# Revit family: MCBII
name_source: partatom
category: 機械設備
units: mm (PartAtom-declared; Revit-internal decimal feet)

## family parameters
OmniClass タイトル = Climate Control (HVAC)
OmniClass 番号 = 23.75.00.00
パーツ タイプ = 標準
ロード時にボイドで切り取り = いいえ
丸型コネクタ寸法 = 直径を使用
作業面ベース = いいえ
共有 = いいえ
常に垂直 = はい
部屋計算ポイント = いいえ

## types (11) — shared parameters
閉（開） = はい
zero-valued in all types: 既定の高さ

## per-type parameters (varying)
| type | H | W | l | t |
| C40x20x10x1.6 | 20  [stored 0.0656168 ft] | 40  [stored 0.131234 ft] | 10  [stored 0.0328084 ft] | 2  [stored 0.00656168 ft] |
| C45x30x10x1.4 | 30  [stored 0.0984252 ft] | 45  [stored 0.147638 ft] | 10  [stored 0.0328084 ft] | 1  [stored 0.00328084 ft] |
| C50x30x10x1.4 | 30  [stored 0.0984252 ft] | 50  [stored 0.164042 ft] | 10  [stored 0.0328084 ft] | 1  [stored 0.00328084 ft] |
| C60x30x10x1.4 | 30  [stored 0.0984252 ft] | 60  [stored 0.19685 ft] | 10  [stored 0.0328084 ft] | 1  [stored 0.00328084 ft] |
| C60x30x10x2.3 | 30  [stored 0.0984252 ft] | 60  [stored 0.19685 ft] | 10  [stored 0.0328084 ft] | 2  [stored 0.00656168 ft] |
| C65x30x10x1.4 | 30  [stored 0.0984252 ft] | 65  [stored 0.213255 ft] | 10  [stored 0.0328084 ft] | 1  [stored 0.00328084 ft] |
| C65x30x10x2.3 | 30  [stored 0.0984252 ft] | 65  [stored 0.213255 ft] | 10  [stored 0.0328084 ft] | 2  [stored 0.00656168 ft] |
| C38x12x1.2 | 12  [stored 0.0393701 ft] | 38  [stored 0.124672 ft] | 5  [stored 0.0164042 ft] | 1  [stored 0.00328084 ft] |
| C38x12x1.6 | 12  [stored 0.0393701 ft] | 38  [stored 0.124672 ft] | 5  [stored 0.0164042 ft] | 2  [stored 0.00656168 ft] |
| C40x20x1.6 | 20  [stored 0.0656168 ft] | 40  [stored 0.131234 ft] | 5  [stored 0.0164042 ft] | 2  [stored 0.00656168 ft] |
| C25x25x5x1.0 | 25  [stored 0.082021 ft] | 25  [stored 0.082021 ft] | 5  [stored 0.0164042 ft] | 1  [stored 0.00328084 ft] |

note: [stored X ft] marks values corroborated as IEEE doubles in the binary element streams (Revit-internal decimal feet)
